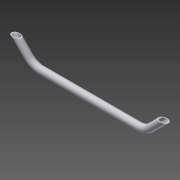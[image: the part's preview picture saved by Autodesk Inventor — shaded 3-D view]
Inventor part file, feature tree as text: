
AUTODESK INVENTOR PART (.ipt)
format: ipt  version: 2015 (Build 190159000, 159)  size: 141,312 bytes
history: native  units: mm
features: sketch x4, other x3, extrude x2, shell x1
ambient origin geometry x8: Origin, YZ Plane, XZ Plane, XY Plane, X Axis, Y Axis, Z Axis, Center Point
bodies: Body1 (feature_tree)
feature tree (10):
  other  "Bryła1"
  extrude  "Wyciągnięcie proste1"  Depth=20.0mm
  shell  "Skorupa1"  Thickness=475.0mm
  other  "Gięcie części1"
  other  "Gięcie części2"
  extrude  "Wyciągnięcie proste2"  Depth=2.0mm
  sketch  "Szkic1"
  sketch  "Szkic2"
  sketch  "Szkic3"
  sketch  "Szkic4"
